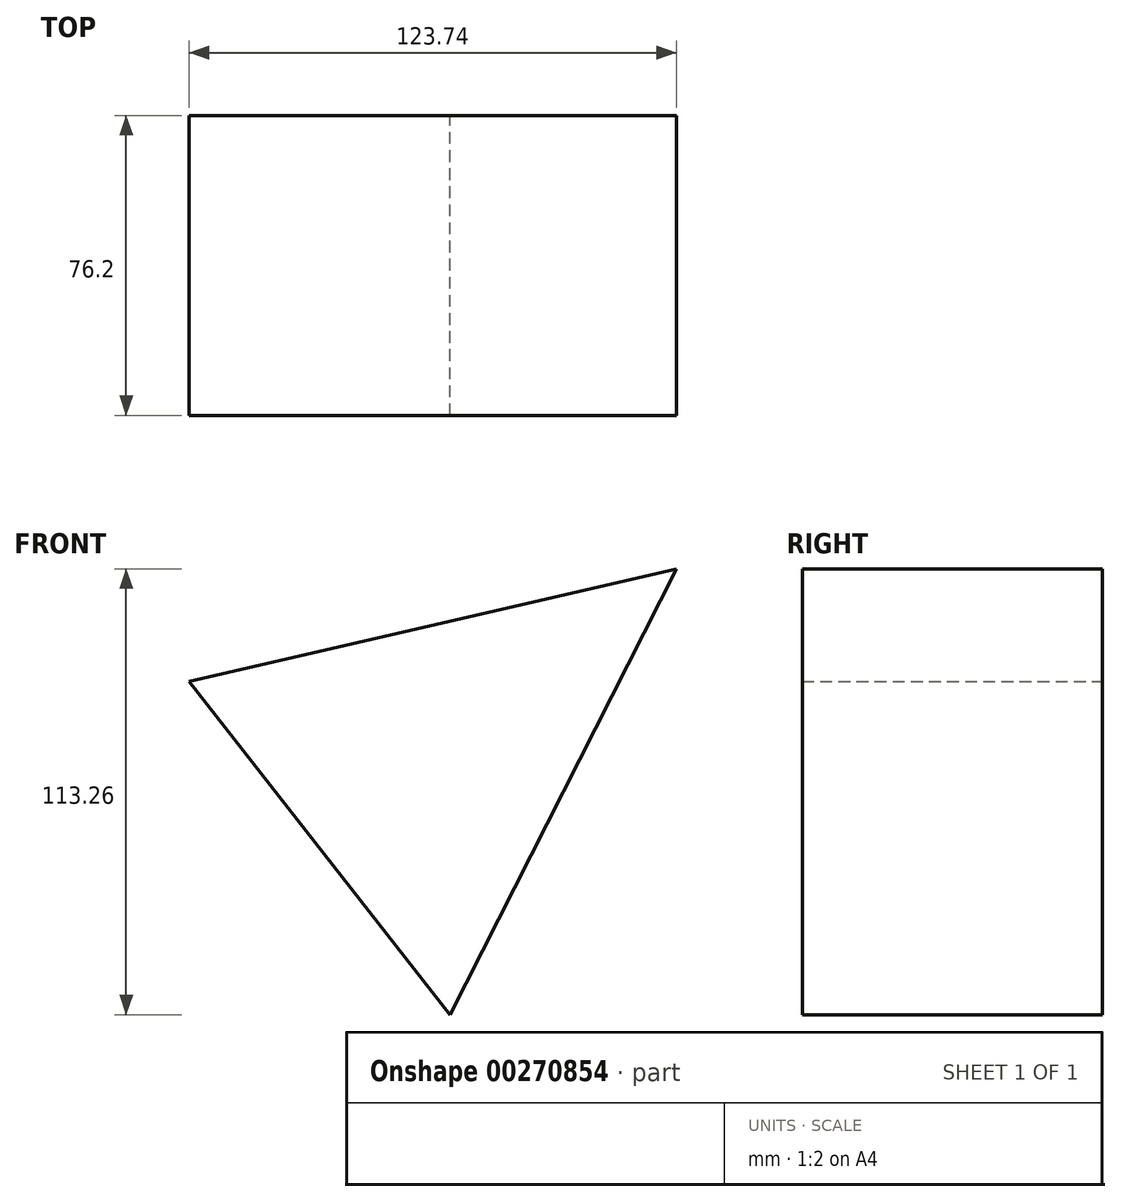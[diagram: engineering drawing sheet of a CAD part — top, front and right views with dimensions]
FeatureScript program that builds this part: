
annotation { "Feature Type Name" : "Feature", "Feature Type Description" : "" }
export const myFeature = defineFeature(function(context is Context, id is Id, definition is map)
    precondition{}
    {
        {
            var Q0;
            Q0=qCreatedBy(makeId("Front.planeOp"),FACE);
            var sketch = newSketch(context, id + "F0", { "sketchPlane" : qUnion([Q0])});
            skLineSegment(sketch, "E0", {"start": v(-64.92, 38.76) * mm, "end": v(1.37, -45.94) * mm});
            skLineSegment(sketch, "E1", {"start": v(-64.92, 38.76) * mm, "end": v(58.82, 67.32) * mm});
            skLineSegment(sketch, "E2", {"start": v(1.37, -45.94) * mm, "end": v(58.82, 67.32) * mm});
            skSolve(sketch);
        }
        {
            var Q0;
            Q0 = qSketchRegion(id + "F0", true);
            extrude(context, id + "F1", {"entities" : qUnion([Q0]), "depth" : 76.2 * mm});
        }
    });
